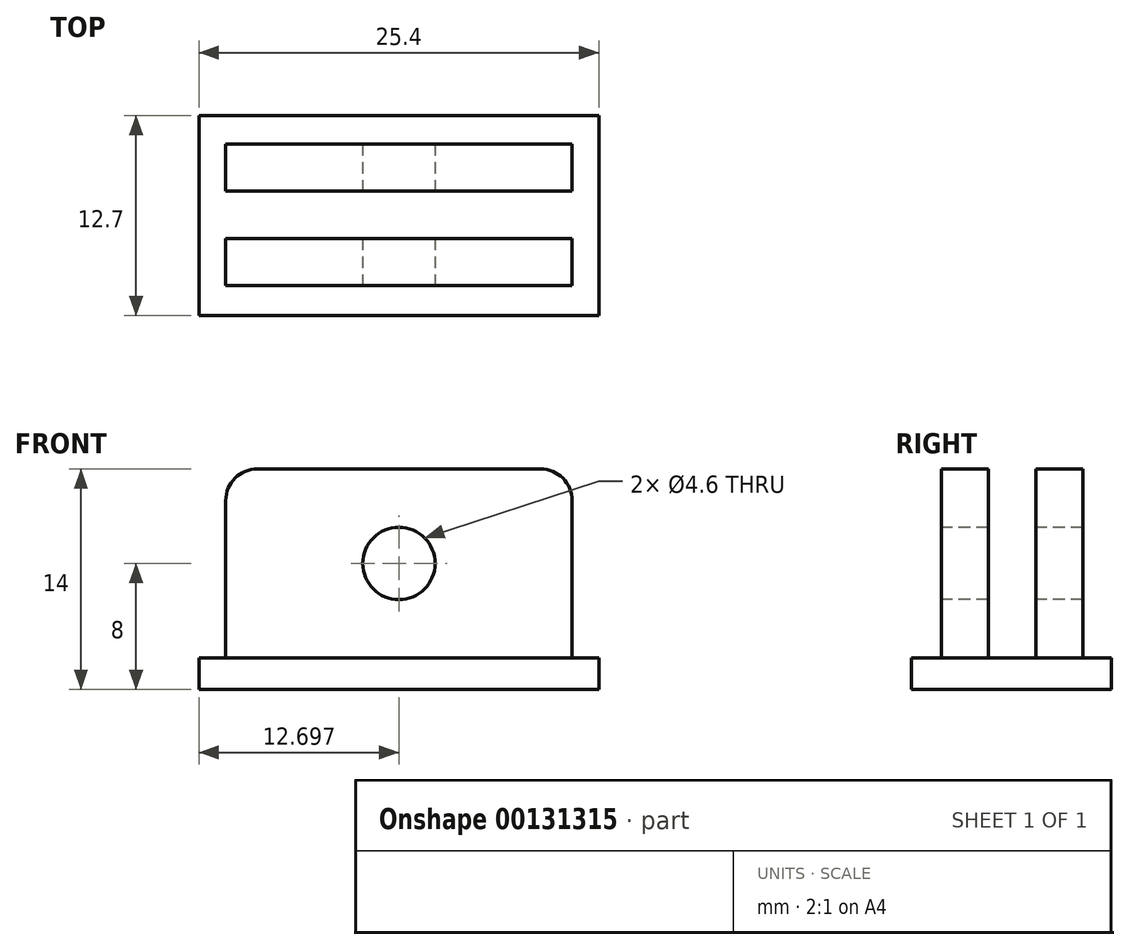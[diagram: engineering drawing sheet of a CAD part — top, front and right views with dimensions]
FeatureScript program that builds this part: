
annotation { "Feature Type Name" : "Feature", "Feature Type Description" : "" }
export const myFeature = defineFeature(function(context is Context, id is Id, definition is map)
    precondition{}
    {
        {
            var Q0;
            Q0=qCreatedBy(makeId("Top.planeOp"),FACE);
            var sketch = newSketch(context, id + "F0", { "sketchPlane" : qUnion([Q0])});
            skLineSegment(sketch, "E0.bottom", {"start": v(4.73, 23.85) * mm, "end": v(30.13, 23.85) * mm});
            skLineSegment(sketch, "E0.top", {"start": v(4.73, 11.15) * mm, "end": v(30.13, 11.15) * mm});
            skLineSegment(sketch, "E0.left", {"start": v(4.73, 23.85) * mm, "end": v(4.73, 11.15) * mm});
            skLineSegment(sketch, "E0.right", {"start": v(30.13, 23.85) * mm, "end": v(30.13, 11.15) * mm});
            skSolve(sketch);
        }
        {
            var Q0;
            Q0 = qSketchRegion(id + "F0", true);
            extrude(context, id + "F1", {"entities" : qUnion([Q0]), "depth" : 2 * mm});
        }
        {
            var Q0;
            Q0=makeQuery(id+"F1.opExtrude","CAP_FACE",FACE,{"disambiguationData":[OSD([sQuery(id+"F0.wireOp",EDGE,"E0.bottom"),sQuery(id+"F0.wireOp",EDGE,"E0.top"),sQuery(id+"F0.wireOp",EDGE,"E0.left"),sQuery(id+"F0.wireOp",EDGE,"E0.right")])],"isStart":false});
            var sketch = newSketch(context, id + "F2", { "sketchPlane" : qUnion([Q0])});
            skLineSegment(sketch, "E1", {"start": v(4.73, 17.5) * mm, "end": v(6.43, 17.5) * mm, "construction": true});
            skLineSegment(sketch, "E2", {"start": v(30.13, 17.5) * mm, "end": v(28.43, 17.5) * mm, "construction": true});
            skLineSegment(sketch, "E3", {"start": v(6.43, 23.85) * mm, "end": v(6.43, 22.05) * mm, "construction": true});
            skLineSegment(sketch, "E4", {"start": v(6.43, 22.05) * mm, "end": v(6.43, 13.05) * mm, "construction": true});
            skLineSegment(sketch, "E5", {"start": v(6.43, 13.05) * mm, "end": v(6.43, 11.15) * mm, "construction": true});
            skLineSegment(sketch, "E6.bottom", {"start": v(6.43, 22.05) * mm, "end": v(28.43, 22.05) * mm});
            skLineSegment(sketch, "E6.top", {"start": v(6.43, 19.05) * mm, "end": v(28.43, 19.05) * mm});
            skLineSegment(sketch, "E6.left", {"start": v(6.43, 22.05) * mm, "end": v(6.43, 19.05) * mm});
            skLineSegment(sketch, "E6.right", {"start": v(28.43, 22.05) * mm, "end": v(28.43, 19.05) * mm});
            skLineSegment(sketch, "E7.bottom", {"start": v(6.43, 13.05) * mm, "end": v(28.43, 13.05) * mm});
            skLineSegment(sketch, "E7.top", {"start": v(6.43, 16.05) * mm, "end": v(28.43, 16.05) * mm});
            skLineSegment(sketch, "E7.left", {"start": v(6.43, 13.05) * mm, "end": v(6.43, 16.05) * mm});
            skLineSegment(sketch, "E7.right", {"start": v(28.43, 13.05) * mm, "end": v(28.43, 16.05) * mm});
            skSolve(sketch);
        }
        {
            var Q0;
            Q0 = qSketchRegion(id + "F2", true);
            extrude(context, id + "F3", {"entities" : qUnion([Q0]), "operationType" : NewBodyOperationType.ADD, "depth" : 12 * mm});
        }
        {
            var Q0;
            Q0=makeQuery(id+"F3.opExtrude","SWEPT_FACE",FACE,{"disambiguationData":[OSD([sQuery(id+"F2.wireOp",EDGE,"E7.bottom")])]});
            var sketch = newSketch(context, id + "F4", { "sketchPlane" : qUnion([Q0])});
            skLineSegment(sketch, "E8", {"start": v(17.43, 14) * mm, "end": v(17.43, 8) * mm, "construction": true});
            skPoint(sketch, "E8.endSnap0", {"position": v(17.43, 14) * mm});
            skCircle(sketch, "E9", {"center": v(17.43, 8) * mm, "radius": 2.3 * mm});
            skSolve(sketch);
        }
        {
            var Q0;
            Q0 = qSketchRegion(id + "F4", true);
            extrude(context, id + "F5", {"entities" : qUnion([Q0]), "operationType" : NewBodyOperationType.REMOVE, "oppositeDirection" : true, "depth" : 25 * mm});
        }
        {
            var Q0;
            Q0=makeQuery(id+"F3.opExtrude","CAP_EDGE",EDGE,{"disambiguationData":[OSD([sQuery(id+"F2.wireOp",EDGE,"E6.left")])],"isStart":false});
            var Q1;
            Q1=makeQuery(id+"F3.opExtrude","CAP_EDGE",EDGE,{"disambiguationData":[OSD([sQuery(id+"F2.wireOp",EDGE,"E7.left")])],"isStart":false});
            var Q2;
            Q2=makeQuery(id+"F3.opExtrude","CAP_EDGE",EDGE,{"disambiguationData":[OSD([sQuery(id+"F2.wireOp",EDGE,"E6.right")])],"isStart":false});
            var Q3;
            Q3=makeQuery(id+"F3.opExtrude","CAP_EDGE",EDGE,{"disambiguationData":[OSD([sQuery(id+"F2.wireOp",EDGE,"E7.right")])],"isStart":false});
            fillet(context, id + "F6", {"entities" : qUnion([Q0, Q1, Q2, Q3]), "radius" : 2 * mm, "tangentPropagation" : true, "allowEdgeOverflow" : false});
        }
    });
